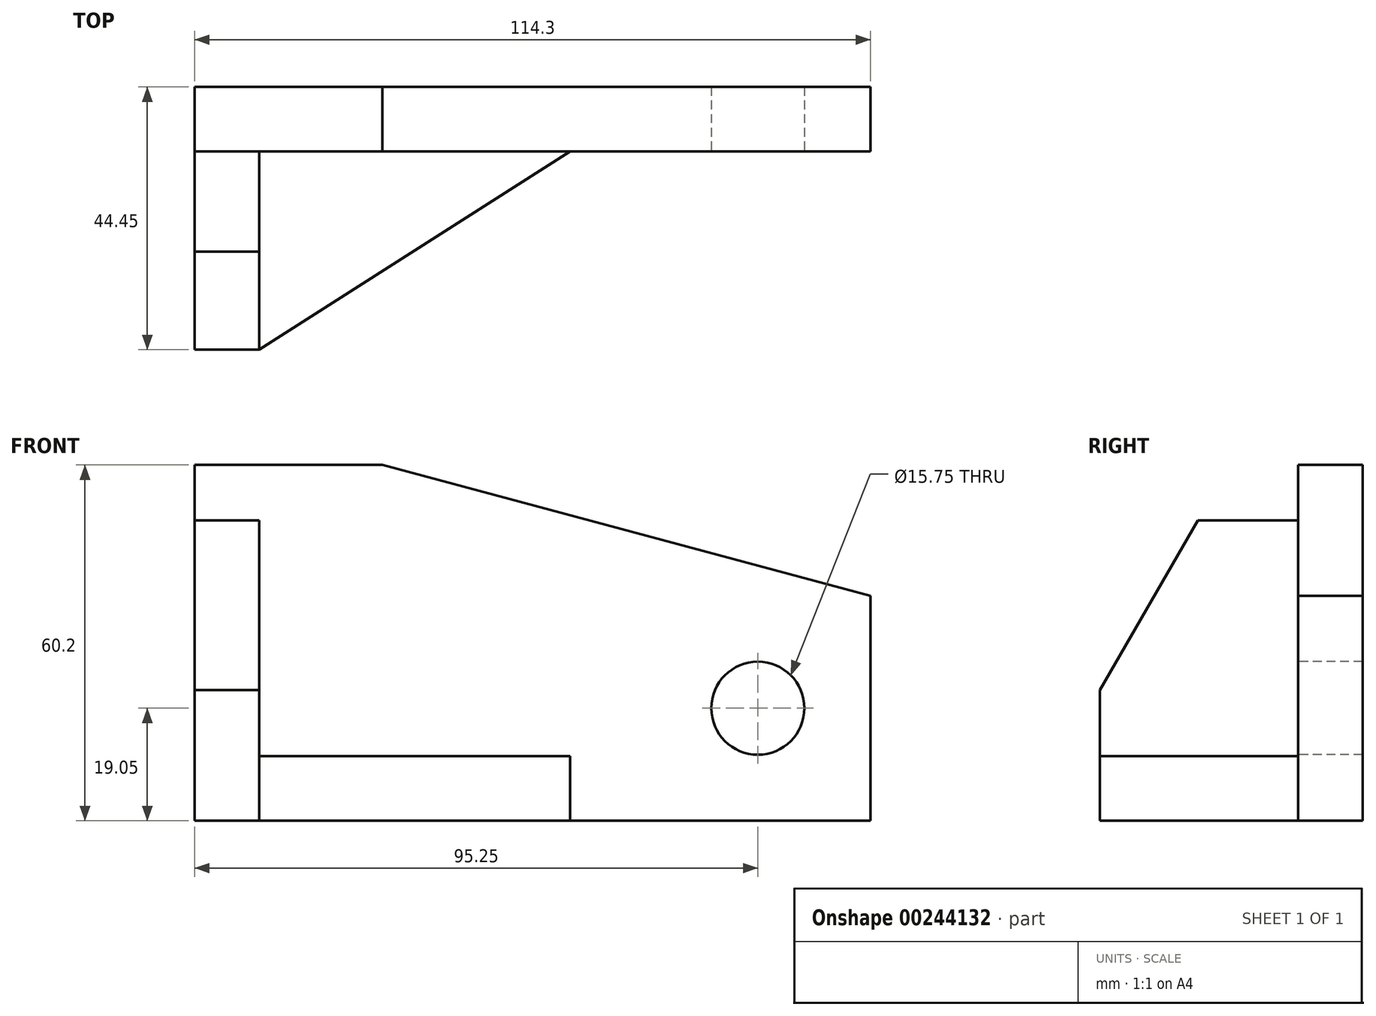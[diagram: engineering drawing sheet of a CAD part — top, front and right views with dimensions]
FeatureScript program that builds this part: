
annotation { "Feature Type Name" : "Feature", "Feature Type Description" : "" }
export const myFeature = defineFeature(function(context is Context, id is Id, definition is map)
    precondition{}
    {
        {
            var Q0;
            Q0=qCreatedBy(makeId("Front.planeOp"),FACE);
            var sketch = newSketch(context, id + "F0", { "sketchPlane" : qUnion([Q0])});
            skLineSegment(sketch, "E0", {"start": v(-59.78, 0) * mm, "end": v(-59.78, 60.2) * mm});
            skLineSegment(sketch, "E1", {"start": v(-59.78, 0) * mm, "end": v(54.52, 0) * mm});
            skLineSegment(sketch, "E2", {"start": v(-59.78, 60.2) * mm, "end": v(-28.03, 60.2) * mm});
            skLineSegment(sketch, "E3", {"start": v(54.52, 38.08) * mm, "end": v(54.52, 0) * mm});
            skLineSegment(sketch, "E4", {"start": v(-28.03, 60.2) * mm, "end": v(54.52, 38.08) * mm});
            skLineSegment(sketch, "E5", {"start": v(-28.03, 60.2) * mm, "end": v(23.24, 60.2) * mm});
            skSolve(sketch);
        }
        {
            var Q0;
            Q0=makeQuery(id+"F0.imprint","IMPRINT",FACE,{"disambiguationData":[TD([[makeQuery(id+"F0.imprint","IMPRINT",EDGE,{"derivedFrom":sQuery(id+"F0.wireOp",EDGE,"E0")}),-1.0]])]});
            extrude(context, id + "F1", {"entities" : qUnion([Q0]), "depth" : 10.92 * mm});
        }
        {
            var Q0;
            Q0=makeQuery(id+"F1.opExtrude","CAP_FACE",FACE,{"disambiguationData":[OSD([sQuery(id+"F0.wireOp",EDGE,"E0"),sQuery(id+"F0.wireOp",EDGE,"E1"),sQuery(id+"F0.wireOp",EDGE,"E2"),sQuery(id+"F0.wireOp",EDGE,"E3"),sQuery(id+"F0.wireOp",EDGE,"E4")])],"isStart":false});
            var sketch = newSketch(context, id + "F2", { "sketchPlane" : qUnion([Q0])});
            skLineSegment(sketch, "E6", {"start": v(-59.78, 0) * mm, "end": v(-59.78, 50.8) * mm});
            skLineSegment(sketch, "E7", {"start": v(-59.78, 0) * mm, "end": v(-48.86, 0) * mm});
            skLineSegment(sketch, "E8", {"start": v(-48.86, 0) * mm, "end": v(-48.86, 50.8) * mm});
            skLineSegment(sketch, "E9", {"start": v(-48.86, 50.8) * mm, "end": v(-59.78, 50.8) * mm});
            skSolve(sketch);
        }
        {
            var Q0;
            Q0=makeQuery(id+"F2.imprint","IMPRINT",FACE,{"disambiguationData":[TD([[makeQuery(id+"F2.imprint","IMPRINT",EDGE,{"derivedFrom":sQuery(id+"F2.wireOp",EDGE,"E6")}),-1.0]])]});
            extrude(context, id + "F3", {"entities" : qUnion([Q0]), "operationType" : NewBodyOperationType.ADD, "depth" : 33.53 * mm});
        }
        {
            var Q0;
            Q0=makeQuery(id+"F3.boolean.opBoolean","MERGE",FACE,{"derivedFrom":[makeQuery(id+"F1.opExtrude","SWEPT_FACE",FACE,{"disambiguationData":[OSD([sQuery(id+"F0.wireOp",EDGE,"E0")])]}),makeQuery(id+"F3.opExtrude","SWEPT_FACE",FACE,{"disambiguationData":[OSD([sQuery(id+"F2.wireOp",EDGE,"E6")])]})]});
            var sketch = newSketch(context, id + "F4", { "sketchPlane" : qUnion([Q0])});
            skLineSegment(sketch, "E10", {"start": v(44.45, 0) * mm, "end": v(44.45, 22.1) * mm});
            skLineSegment(sketch, "E11", {"start": v(44.45, 22.1) * mm, "end": v(27.88, 50.8) * mm});
            skSolve(sketch);
        }
        {
            var Q0;
            {var subQ0=sQuery(id+"F4.wireOp",EDGE,"E11");Q0=makeQuery(id+"F4.imprint","IMPRINT",FACE,{"disambiguationData":[TD([[makeQuery(id+"F4.imprint","IMPRINT",EDGE,{"derivedFrom":subQ0}),-1.0]])]});}
            extrude(context, id + "F5", {"entities" : qUnion([Q0]), "operationType" : NewBodyOperationType.REMOVE, "oppositeDirection" : true, "depth" : 10.92 * mm});
        }
        {
            var Q0;
            Q0=makeQuery(id+"F1.opExtrude","CAP_FACE",FACE,{"disambiguationData":[OSD([sQuery(id+"F0.wireOp",EDGE,"E0"),sQuery(id+"F0.wireOp",EDGE,"E1"),sQuery(id+"F0.wireOp",EDGE,"E2"),sQuery(id+"F0.wireOp",EDGE,"E3"),sQuery(id+"F0.wireOp",EDGE,"E4")])],"isStart":false});
            var sketch = newSketch(context, id + "F6", { "sketchPlane" : qUnion([Q0])});
            skLineSegment(sketch, "E12", {"start": v(-48.86, 0) * mm, "end": v(-48.86, 10.92) * mm});
            skLineSegment(sketch, "E13", {"start": v(-48.86, 0) * mm, "end": v(3.72, 0) * mm});
            skLineSegment(sketch, "E14", {"start": v(3.72, 0) * mm, "end": v(3.72, 10.92) * mm});
            skLineSegment(sketch, "E15", {"start": v(3.72, 10.92) * mm, "end": v(-48.86, 10.92) * mm});
            skSolve(sketch);
        }
        {
            var Q0;
            Q0=makeQuery(id+"F6.imprint","IMPRINT",FACE,{"disambiguationData":[TD([[makeQuery(id+"F6.imprint","IMPRINT",EDGE,{"derivedFrom":sQuery(id+"F6.wireOp",EDGE,"E12")}),-1.0]])]});
            extrude(context, id + "F7", {"entities" : qUnion([Q0]), "operationType" : NewBodyOperationType.ADD, "depth" : 33.53 * mm});
        }
        {
            var Q0;
            Q0=makeQuery(id+"F7.opExtrude","SWEPT_FACE",FACE,{"disambiguationData":[OSD([sQuery(id+"F6.wireOp",EDGE,"E15")])]});
            var sketch = newSketch(context, id + "F8", { "sketchPlane" : qUnion([Q0])});
            skLineSegment(sketch, "E16", {"start": v(-48.86, -44.45) * mm, "end": v(3.72, -10.92) * mm});
            skSolve(sketch);
        }
        {
            var Q0;
            Q0=makeQuery(id+"F8.imprint","IMPRINT",FACE,{"disambiguationData":[TD([[makeQuery(id+"F8.imprint","IMPRINT",EDGE,{"derivedFrom":sQuery(id+"F8.wireOp",EDGE,"E16")}),-1.0]])]});
            extrude(context, id + "F9", {"entities" : qUnion([Q0]), "operationType" : NewBodyOperationType.REMOVE, "oppositeDirection" : true, "depth" : 10.92 * mm});
        }
        {
            var Q0;
            Q0=makeQuery(id+"F1.opExtrude","CAP_FACE",FACE,{"disambiguationData":[OSD([sQuery(id+"F0.wireOp",EDGE,"E0"),sQuery(id+"F0.wireOp",EDGE,"E1"),sQuery(id+"F0.wireOp",EDGE,"E2"),sQuery(id+"F0.wireOp",EDGE,"E3"),sQuery(id+"F0.wireOp",EDGE,"E4")])],"isStart":false});
            var sketch = newSketch(context, id + "F10", { "sketchPlane" : qUnion([Q0])});
            skCircle(sketch, "E17", {"center": v(35.47, 19.05) * mm, "radius": 7.87 * mm});
            skPoint(sketch, "E18", {"position": v(35.47, 0) * mm});
            skLineSegment(sketch, "E19", {"start": v(35.47, 19.05) * mm, "end": v(35.47, 0) * mm});
            skLineSegment(sketch, "E20", {"start": v(35.47, 0) * mm, "end": v(54.52, 0) * mm});
            skSolve(sketch);
        }
        {
            var Q0;
            Q0=makeQuery(id+"F10.imprint","IMPRINT",FACE,{"disambiguationData":[TD([[makeQuery(id+"F10.imprint","IMPRINT",EDGE,{"derivedFrom":sQuery(id+"F10.wireOp",EDGE,"E17")}),1.0]])]});
            extrude(context, id + "F11", {"entities" : qUnion([Q0]), "operationType" : NewBodyOperationType.REMOVE, "oppositeDirection" : true, "depth" : 10.92 * mm});
        }
    });
